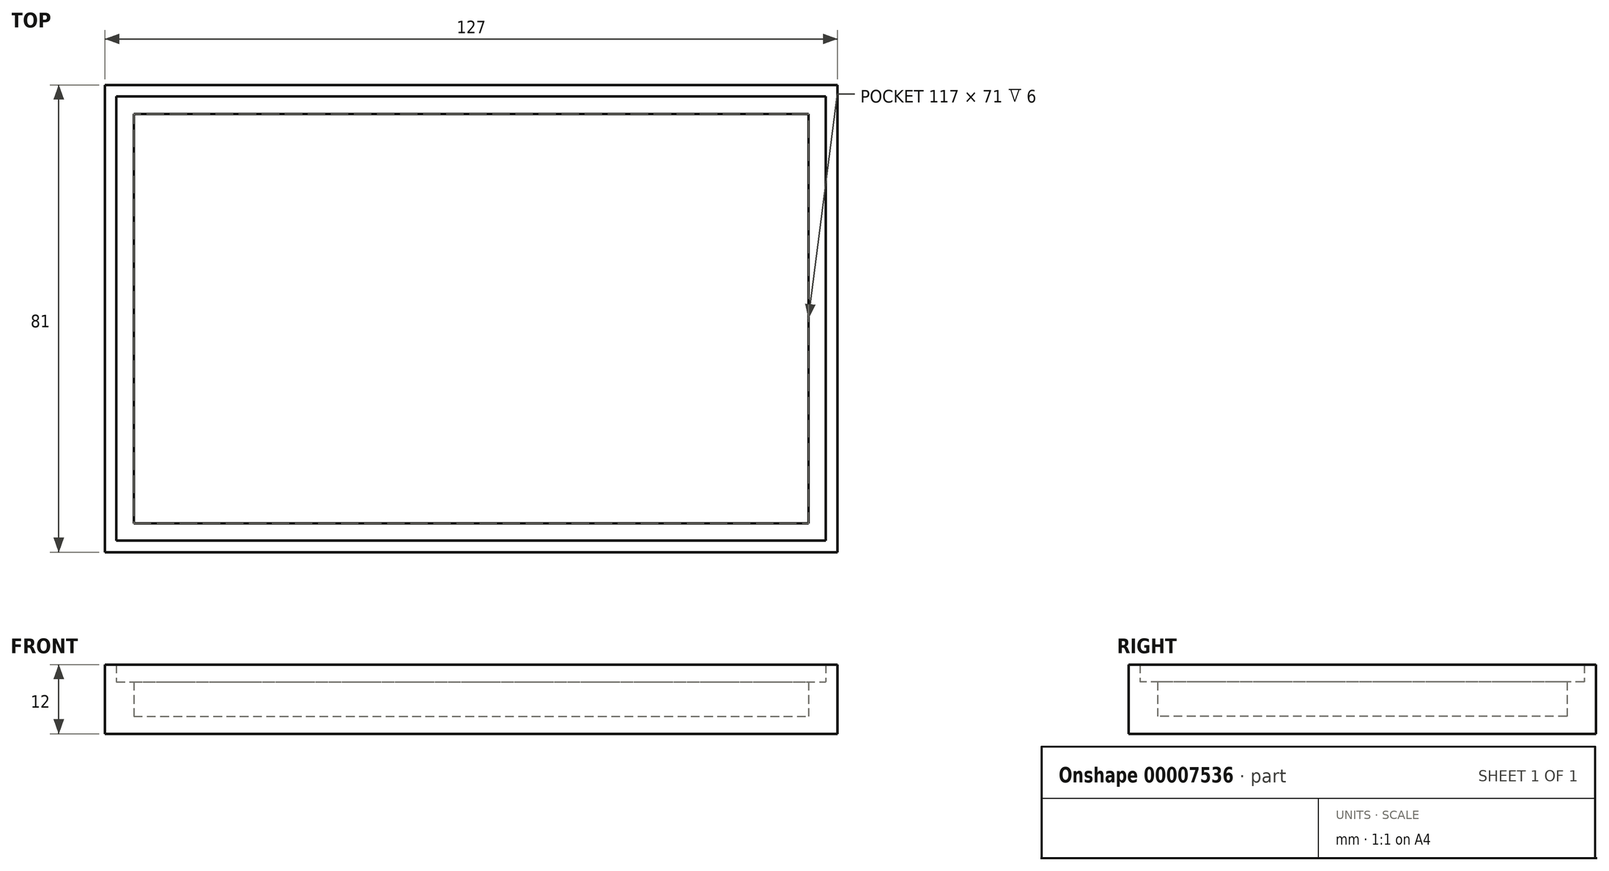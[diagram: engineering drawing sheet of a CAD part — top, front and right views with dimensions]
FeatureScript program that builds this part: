
annotation { "Feature Type Name" : "Feature", "Feature Type Description" : "" }
export const myFeature = defineFeature(function(context is Context, id is Id, definition is map)
    precondition{}
    {
        {
            var Q0;
            Q0=qCreatedBy(makeId("Top.planeOp"),FACE);
            var sketch = newSketch(context, id + "F0", { "sketchPlane" : qUnion([Q0])});
            skLineSegment(sketch, "E0.bottom", {"start": v(-55.28, 38.95) * mm, "end": v(71.72, 38.95) * mm});
            skLineSegment(sketch, "E0.top", {"start": v(-55.28, -42.05) * mm, "end": v(71.72, -42.05) * mm});
            skLineSegment(sketch, "E0.left", {"start": v(-55.28, 38.95) * mm, "end": v(-55.28, -42.05) * mm});
            skLineSegment(sketch, "E0.right", {"start": v(71.72, 38.95) * mm, "end": v(71.72, -42.05) * mm});
            skLineSegment(sketch, "E1.0", {"start": v(-50.28, 33.95) * mm, "end": v(66.72, 33.95) * mm});
            skLineSegment(sketch, "E1.1", {"start": v(-50.28, 33.95) * mm, "end": v(-50.28, -37.05) * mm});
            skLineSegment(sketch, "E1.2", {"start": v(-50.28, -37.05) * mm, "end": v(66.72, -37.05) * mm});
            skLineSegment(sketch, "E1.3", {"start": v(66.72, 33.95) * mm, "end": v(66.72, -37.05) * mm});
            skLineSegment(sketch, "E2.0", {"start": v(-53.28, 36.95) * mm, "end": v(69.72, 36.95) * mm});
            skLineSegment(sketch, "E2.1", {"start": v(-53.28, 36.95) * mm, "end": v(-53.28, -40.05) * mm});
            skLineSegment(sketch, "E2.2", {"start": v(-53.28, -40.05) * mm, "end": v(69.72, -40.05) * mm});
            skLineSegment(sketch, "E2.3", {"start": v(69.72, 36.95) * mm, "end": v(69.72, -40.05) * mm});
            skSolve(sketch);
        }
        {
            var Q0;
            Q0=makeQuery(id+"F0.imprint","IMPRINT",FACE,{"disambiguationData":[TD([[makeQuery(id+"F0.imprint","IMPRINT",EDGE,{"derivedFrom":sQuery(id+"F0.wireOp",EDGE,"E1.0")}),1.0]])]});
            extrude(context, id + "F1", {"entities" : qUnion([Q0]), "depth" : 9 * mm});
        }
        {
            var Q0;
            Q0 = qSketchRegion(id + "F0", true);
            extrude(context, id + "F2", {"entities" : qUnion([Q0]), "operationType" : NewBodyOperationType.ADD, "depth" : 12 * mm});
        }
        {
            var Q0;
            Q0=makeQuery(id+"F0.imprint","IMPRINT",FACE,{"disambiguationData":[TD([[makeQuery(id+"F0.imprint","IMPRINT",EDGE,{"derivedFrom":sQuery(id+"F0.wireOp",EDGE,"E1.0")}),-1.0]])]});
            extrude(context, id + "F3", {"entities" : qUnion([Q0]), "operationType" : NewBodyOperationType.ADD, "depth" : 3 * mm});
        }
    });
